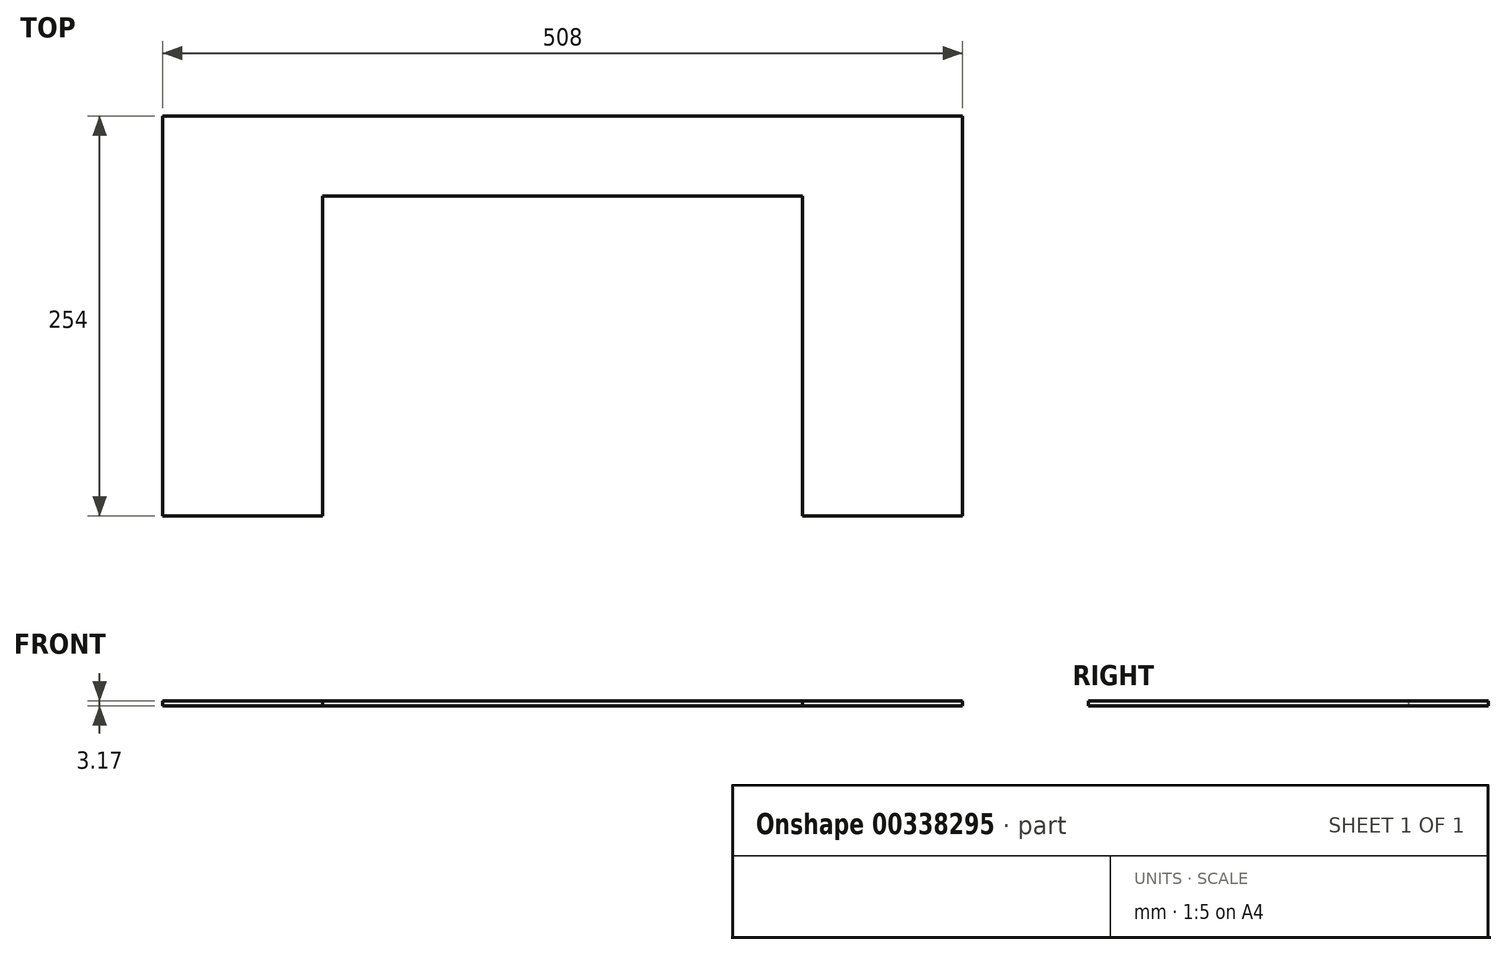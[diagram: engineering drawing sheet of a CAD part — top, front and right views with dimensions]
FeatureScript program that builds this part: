
annotation { "Feature Type Name" : "Feature", "Feature Type Description" : "" }
export const myFeature = defineFeature(function(context is Context, id is Id, definition is map)
    precondition{}
    {
        {
            var Q0;
            Q0=qCreatedBy(makeId("Top.planeOp"),FACE);
            var sketch = newSketch(context, id + "F0", { "sketchPlane" : qUnion([Q0])});
            skLineSegment(sketch, "E0.bottom", {"start": v(0, 0) * mm, "end": v(101.6, 0) * mm});
            skLineSegment(sketch, "E0.left", {"start": v(0, 0) * mm, "end": v(0, 254) * mm});
            skLineSegment(sketch, "E0.right", {"start": v(101.6, 0) * mm, "end": v(101.6, 203.2) * mm});
            skLineSegment(sketch, "E1.bottom", {"start": v(101.6, 203.2) * mm, "end": v(406.4, 203.2) * mm});
            skLineSegment(sketch, "E1.top", {"start": v(0, 254) * mm, "end": v(508, 254) * mm});
            skLineSegment(sketch, "E2.top", {"start": v(406.4, 0) * mm, "end": v(508, 0) * mm});
            skLineSegment(sketch, "E2.left", {"start": v(406.4, 203.2) * mm, "end": v(406.4, 0) * mm});
            skLineSegment(sketch, "E2.right", {"start": v(508, 254) * mm, "end": v(508, 0) * mm});
            skLineSegment(sketch, "E3", {"start": v(254, 203.2) * mm, "end": v(254, 254) * mm, "construction": true});
            skSolve(sketch);
        }
        {
            var Q0;
            Q0 = qSketchRegion(id + "F0", true);
            extrude(context, id + "F1", {"entities" : qUnion([Q0]), "depth" : 3.17 * mm});
        }
    });
